# Revit family: Беседка «София» Арт 14947
name_source: partatom
category: Антураж
revit_build: Autodesk Revit 2018 (Build: 20180423_1000(x64)
units: mm (PartAtom-declared; Revit-internal decimal feet)

## family parameters
Всегда вертикально = Да
Источник визуального образа = Геометрия семейства
На основе рабочей плоскости = Нет
Общий = Нет
При загрузке вырезать с полостями = Нет
Точка расчета площади = Нет

## types (2) — shared parameters
URL = https://hobbyka.ru
Артикул товара = Арт. 14947
Высота = 2790 мм
Группа модели = Навесы и беседки
Длина = 4000 мм
Изготовитель = ООО «Хоббика»
Материал изделия = Дерево, поликарбонат
Цвет крыши = Поликарбанат
Ширина = 3000 мм

## per-type parameters (varying)
| type | Изображение типоразмера | Лиственница | Сосна | Цвет каркаса |
| Беседка «София». Версия стандарт сосна | Беседка «София». Версия стандарт сосна Арт 14947.jpg | Нет | Да | Дерево сосна |
| Беседка «София». Версия стандарт лиственница | Беседка «София». Версия стандарт лиственница Арт 14947.jpg | Да | Нет | Дерево лиственница |

note: column(s) folded — value = type name in every type: Описание
